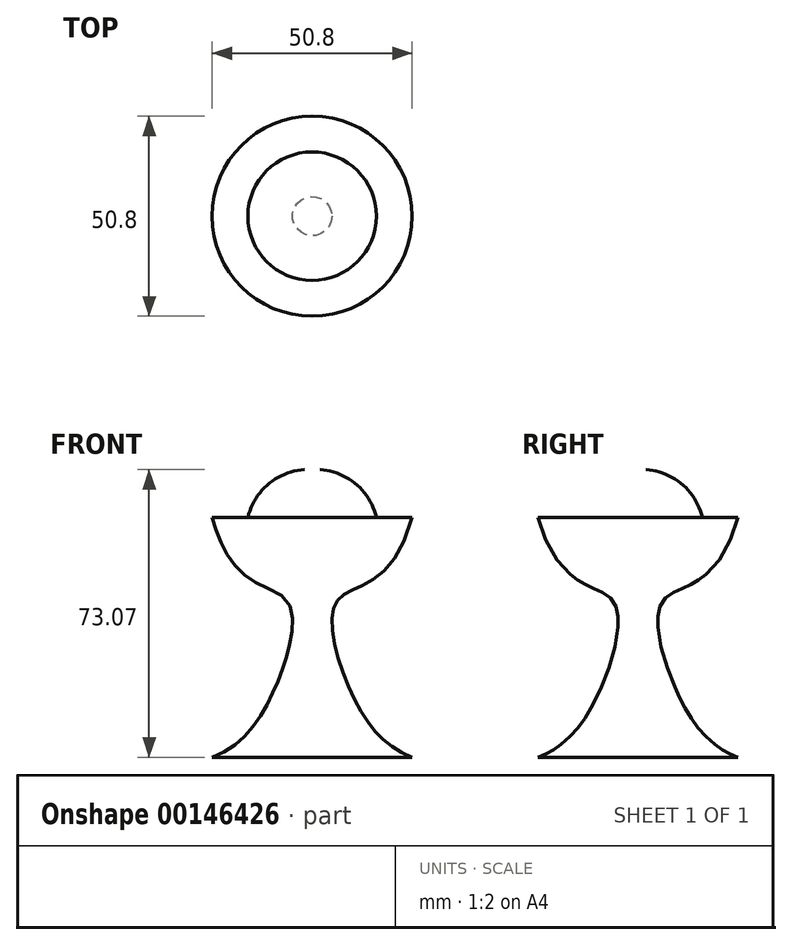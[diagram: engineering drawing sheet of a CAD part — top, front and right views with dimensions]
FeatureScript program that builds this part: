
annotation { "Feature Type Name" : "Feature", "Feature Type Description" : "" }
export const myFeature = defineFeature(function(context is Context, id is Id, definition is map)
    precondition{}
    {
        {
            var Q0;
            Q0=qCreatedBy(makeId("Top.planeOp"),FACE);
            var sketch = newSketch(context, id + "F0", { "sketchPlane" : qUnion([Q0])});
            skCircle(sketch, "E0", {"center": v(0, 0) * mm, "radius": 25.4 * mm});
            skSolve(sketch);
        }
        {
            var Q0;
            Q0 = qSketchRegion(id + "F0", true);
            extrude(context, id + "F1", {"entities" : qUnion([Q0]), "depth" : 60.96 * mm});
        }
        {
            var Q0;
            Q0=qCreatedBy(makeId("Front.planeOp"),FACE);
            var sketch = newSketch(context, id + "F2", { "sketchPlane" : qUnion([Q0])});
            skLineSegment(sketch, "E1", {"start": v(-25.4, 65.52) * mm, "end": v(-25.4, -17.55) * mm, "construction": true});
            skLineSegment(sketch, "E2", {"start": v(0, 65.52) * mm, "end": v(0, -17.55) * mm, "construction": true});
            skLineSegment(sketch, "E3", {"start": v(-64.9, 60.96) * mm, "end": v(64.09, 60.96) * mm, "construction": true});
            skFitSpline(sketch, "E4", {"points": [v(-25.4, 60.96) * mm, v(-6.12, 39.4) * mm, v(-10.82, 14.7) * mm, v(-25.4, 0) * mm], "startDerivative": vector(42.72, -160.2) * mm, "endDerivative": vector(-66.1, -25.7) * mm});
            skLineSegment(sketch, "E5", {"start": v(-25.4, 60.96) * mm, "end": v(-25.4, 0) * mm});
            skSolve(sketch);
        }
        {
            var Q0;
            Q0 = qSketchRegion(id + "F2", true);
            var Q1;
            Q1=sQuery(id+"F2.wireOp",EDGE,"E2");
            revolve(context, id + "F3", {"operationType" : NewBodyOperationType.REMOVE, "entities" : qUnion([Q0]), "axis" : qUnion([Q1]), "revolveType" : RevolveType.FULL});
        }
        {
            var Q0;
            Q0=qCreatedBy(makeId("Front.planeOp"),FACE);
            var sketch = newSketch(context, id + "F4", { "sketchPlane" : qUnion([Q0])});
            skArc(sketch, "E6", {"start": v(0, 41.64) * mm, "mid": v(16.74, 57.35) * mm, "end": v(0, 73.07) * mm});
            skLineSegment(sketch, "E7", {"start": v(0, 73.07) * mm, "end": v(0, 41.64) * mm});
            skSolve(sketch);
        }
        {
            var Q0;
            Q0 = qSketchRegion(id + "F4", true);
            var Q1;
            Q1=sQuery(id+"F4.wireOp",EDGE,"E7");
            revolve(context, id + "F5", {"operationType" : NewBodyOperationType.REMOVE, "entities" : qUnion([Q0]), "axis" : qUnion([Q1]), "revolveType" : RevolveType.FULL, "oppositeDirection" : true});
        }
    });
